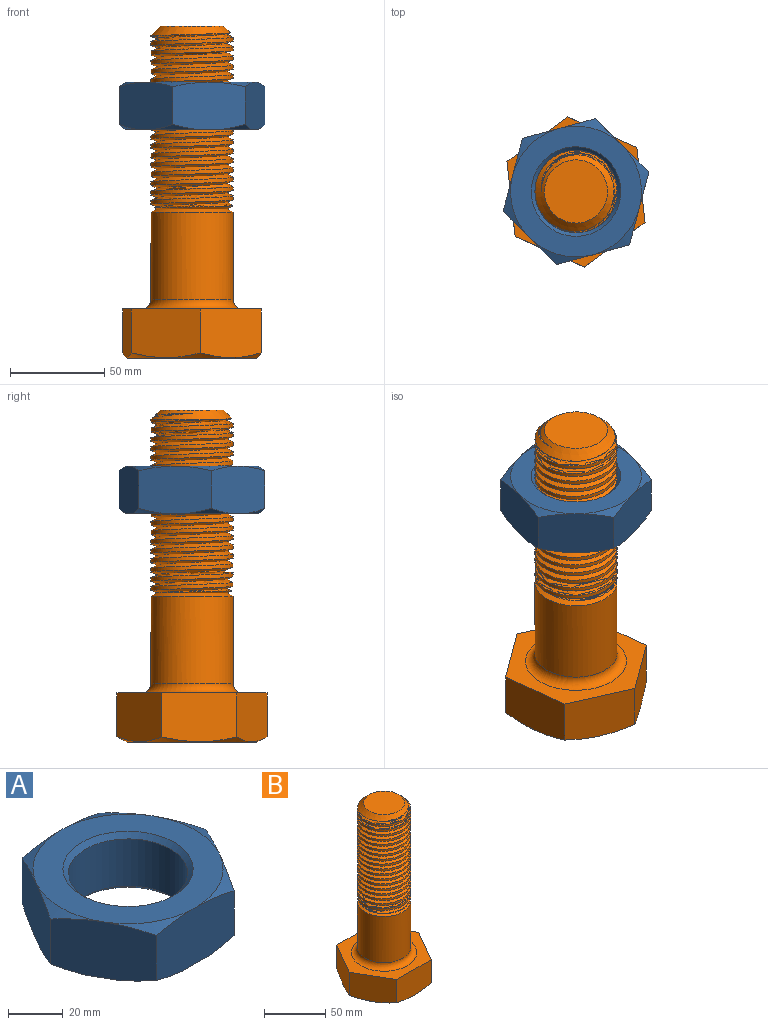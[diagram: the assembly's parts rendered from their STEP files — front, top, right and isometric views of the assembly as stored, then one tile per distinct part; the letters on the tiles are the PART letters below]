
ASSEMBLY  parts=2 mates=1
PART A: 23 faces, bbox 80x80x25 mm
  f0: plane 34.65x25.01mm, normal (-0.87,0.5,0), area 938.1mm2, adj f1,f5,f6,f7,f14,f15,f19,f20
  f1: plane 34.65x25.01mm, normal (-0.87,-0.5,0), area 938.1mm2, adj f0,f2,f6,f7,f13,f14,f20,f21
  f2: plane 40.01x25.01mm, normal (0,-1,0), area 938.1mm2, adj f1,f3,f6,f7,f12,f13,f21,f22
  f3: plane 34.65x25.01mm, normal (0.87,-0.5,0), area 938.1mm2, adj f2,f4,f6,f7,f11,f12,f17,f22
  f4: plane 34.65x25.01mm, normal (0.87,0.5,0), area 938.1mm2, adj f3,f5,f6,f7,f11,f16,f17,f18
  f5: plane 40.01x25.01mm, normal (0,1,0), area 938.1mm2, adj f0,f4,f6,f7,f15,f16,f18,f19
  f6: plane 69.32x69.28mm, normal (0,0,1), area 2001.7mm2, adj f0,f1,f2,f3,f4,f5,f9,f17
  f7: plane 70.54x69.28mm, normal (0,0,-1), area 2102.8mm2, adj f0,f1,f2,f3,f4,f5,f10,f11
  f8: cylinder r=21.75mm len=43.5mm, axis (0,0,1), area 2869.8mm2, adj f9,f10
  f9: cone r=21.75mm half-angle=45deg, axis (0,0,1), area 404.3mm2, adj f6,f8
  f10: cone r=23.75mm half-angle=45deg, axis (0,0,-1), area 404.3mm2, adj f7,f8
  f11: cone r=33.52mm half-angle=61.5deg, axis (0,0,1), area 53.5mm2, adj f3,f4,f7
  f12: cone r=33.52mm half-angle=61.5deg, axis (0,0,1), area 53.5mm2, adj f2,f3,f7
  f13: cone r=33.52mm half-angle=61.5deg, axis (0,0,1), area 53.5mm2, adj f1,f2,f7
  f14: cone r=33.52mm half-angle=61.5deg, axis (0,0,1), area 53.5mm2, adj f0,f1,f7
  f15: cone r=33.52mm half-angle=61.5deg, axis (0,0,1), area 53.5mm2, adj f0,f5,f7
  f16: cone r=33.52mm half-angle=61.5deg, axis (0,0,1), area 53.5mm2, adj f4,f5,f7
  f17: cone r=33.52mm half-angle=65.9deg, axis (0,0,-1), area 70mm2, adj f3,f4,f6
  f18: cone r=33.52mm half-angle=65.9deg, axis (0,0,-1), area 70mm2, adj f4,f5,f6
  f19: cone r=33.52mm half-angle=65.9deg, axis (0,0,-1), area 70mm2, adj f0,f5,f6
  f20: cone r=33.52mm half-angle=65.9deg, axis (0,0,-1), area 70mm2, adj f0,f1,f6
  f21: cone r=33.52mm half-angle=65.9deg, axis (0,0,-1), area 70mm2, adj f1,f2,f6
  f22: cone r=33.52mm half-angle=65.9deg, axis (0,0,-1), area 70mm2, adj f2,f3,f6
PART B: 18 faces, bbox 80x80x176.8 mm
  f0: plane 34.64x25.86mm, normal (-0.87,0.5,0), area 999.2mm2, adj f1,f5,f6,f8
  f1: plane 34.64x25.86mm, normal (-0.87,-0.5,0), area 999.2mm2, adj f0,f2,f6,f8
  f2: plane 40.01x25.86mm, normal (0,-1,0), area 999.2mm2, adj f1,f3,f6,f8
  f3: plane 34.64x25.86mm, normal (0.87,-0.5,0), area 999.2mm2, adj f2,f4,f6,f8
  f4: plane 34.64x25.86mm, normal (0.87,0.5,0), area 999.2mm2, adj f3,f5,f6,f8
  f5: plane 40.01x25.86mm, normal (0,1,0), area 999.2mm2, adj f0,f4,f6,f8
  f6: plane 80x69.28mm, normal (0,0,1), area 1908.9mm2, adj f0,f1,f2,f3,f4,f5,f10
  f7: cylinder r=21.75mm len=46.34mm, axis (0,0,-1), area 6332.8mm2, adj f10,f12
  f8: cone r=33.14mm half-angle=64.5deg, axis (0,0,1), area 501.4mm2, adj f0,f1,f2,f3,f4,f5,f9
  f9: plane 68.68x68.68mm, normal (0,0,-1), area 3704.3mm2, adj f8
  f10: torus R=26.75mm, axis (0,0,1), area 1163mm2, adj f6,f7
  f11: cone r=18.45mm half-angle=70.7deg, axis (0,0,1), area 307.9mm2, adj f12,f15,f16,f17
  f12: cone r=21.75mm half-angle=62deg, axis (0,0,-1), area 472mm2, adj f7,f11
  f13: plane 33.5x33.5mm, normal (0,0,1), area 881.4mm2, adj f14
  f14: cone r=16.75mm half-angle=45deg, axis (0,0,-1), area 677.3mm2, adj f13,f15,f16,f17
  f15: bspline ~97.66x55.56mm, area 8275.9mm2, adj f11,f14,f16,f17
  f16: bspline ~98.69x55.56mm, area 8874mm2, adj f11,f14,f15,f17
  f17: cylinder r=21.75mm len=90.75mm, axis (0,0,-1), area 6802.4mm2, adj f11,f14,f15,f16
PLACE A rot(axis=(0,0,1),75.1deg) t=(-80.04,28.81,120.3)mm
PLACE B rot(axis=(0,0,1),96.2deg) t=(-80.04,28.81,-0.91)mm fixed
MATE cylindrical A.f8 <-> B.f7  axis (0,0,1) through (-80.04,28.81,145.3)mm
